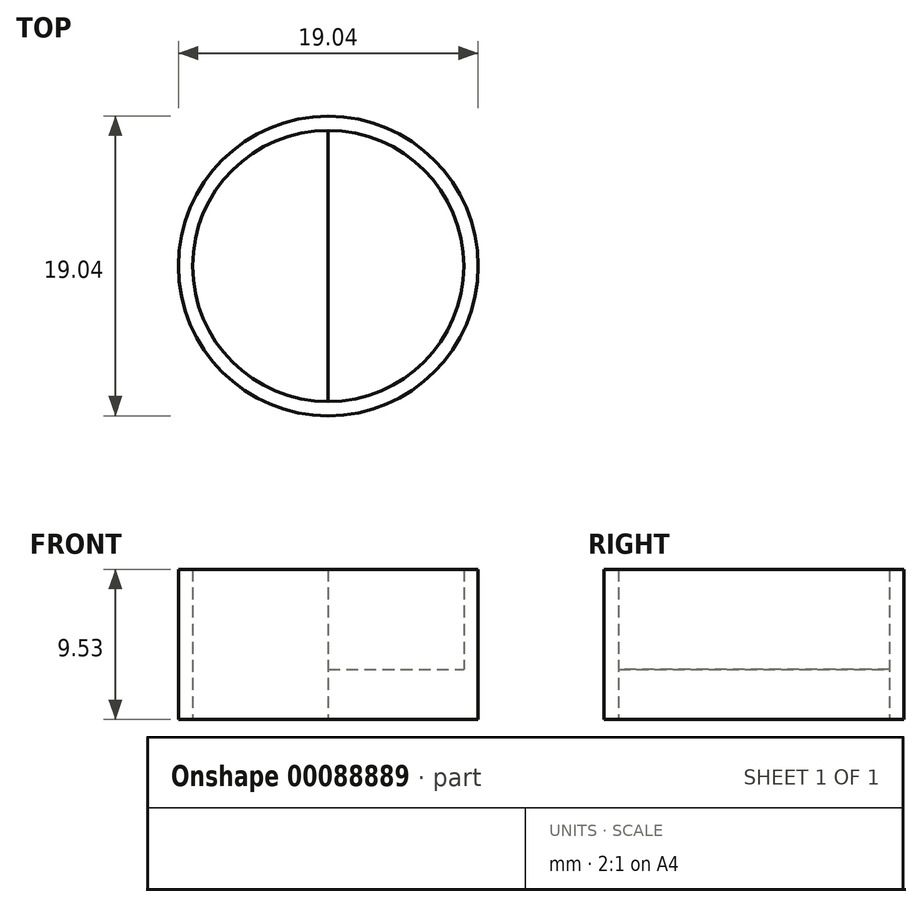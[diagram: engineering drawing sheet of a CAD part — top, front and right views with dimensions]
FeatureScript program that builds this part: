
annotation { "Feature Type Name" : "Feature", "Feature Type Description" : "" }
export const myFeature = defineFeature(function(context is Context, id is Id, definition is map)
    precondition{}
    {
        {
            var Q0;
            Q0=qCreatedBy(makeId("Top.planeOp"),FACE);
            var sketch = newSketch(context, id + "F0", { "sketchPlane" : qUnion([Q0])});
            skCircle(sketch, "E0", {"center": v(0, 0) * mm, "radius": 8.61 * mm});
            skCircle(sketch, "E1", {"center": v(0, 0) * mm, "radius": 9.52 * mm});
            skLineSegment(sketch, "E2", {"start": v(0, 8.61) * mm, "end": v(0, -8.61) * mm});
            skSolve(sketch);
        }
        {
            var Q0;
            {var subQ0=sQuery(id+"F0.wireOp",EDGE,"E2");Q0=makeQuery(id+"F0.imprint","IMPRINT",FACE,{"disambiguationData":[TD([[makeQuery(id+"F0.imprint","IMPRINT",EDGE,{"derivedFrom":subQ0}),1.0]])]});}
            var Q1;
            Q1=makeQuery(id+"F0.imprint","IMPRINT",FACE,{"disambiguationData":[TD([[makeQuery(id+"F0.imprint","IMPRINT",EDGE,{"derivedFrom":sQuery(id+"F0.wireOp",EDGE,"E1")}),1.0]])]});
            extrude(context, id + "F1", {"entities" : qUnion([Q0, Q1]), "depth" : 3.17 * mm});
        }
        {
            var Q0;
            Q0=makeQuery(id+"F1.opExtrude","CAP_FACE",FACE,{"disambiguationData":[OSD([sQuery(id+"F0.wireOp",EDGE,"E0"),sQuery(id+"F0.wireOp",EDGE,"E1"),sQuery(id+"F0.wireOp",EDGE,"E2")])],"isStart":false});
            var sketch = newSketch(context, id + "F2", { "sketchPlane" : qUnion([Q0])});
            skCircle(sketch, "E3", {"center": v(0, 0) * mm, "radius": 8.6 * mm});
            skSolve(sketch);
        }
        {
            var Q0;
            {var subQ1=makeQuery(id+"F1.opExtrude","CAP_EDGE",EDGE,{"disambiguationData":[OSD([sQuery(id+"F0.wireOp",EDGE,"E0")])],"isStart":false});Q0=makeQuery(id+"F2.imprint","IMPRINT",FACE,{"disambiguationData":[TD([[makeQuery(id+"F2.imprint","IMPRINT",EDGE,{"derivedFrom":subQ1}),-1.0]])]});}
            extrude(context, id + "F3", {"entities" : qUnion([Q0]), "operationType" : NewBodyOperationType.ADD, "depth" : 6.35 * mm});
        }
    });
